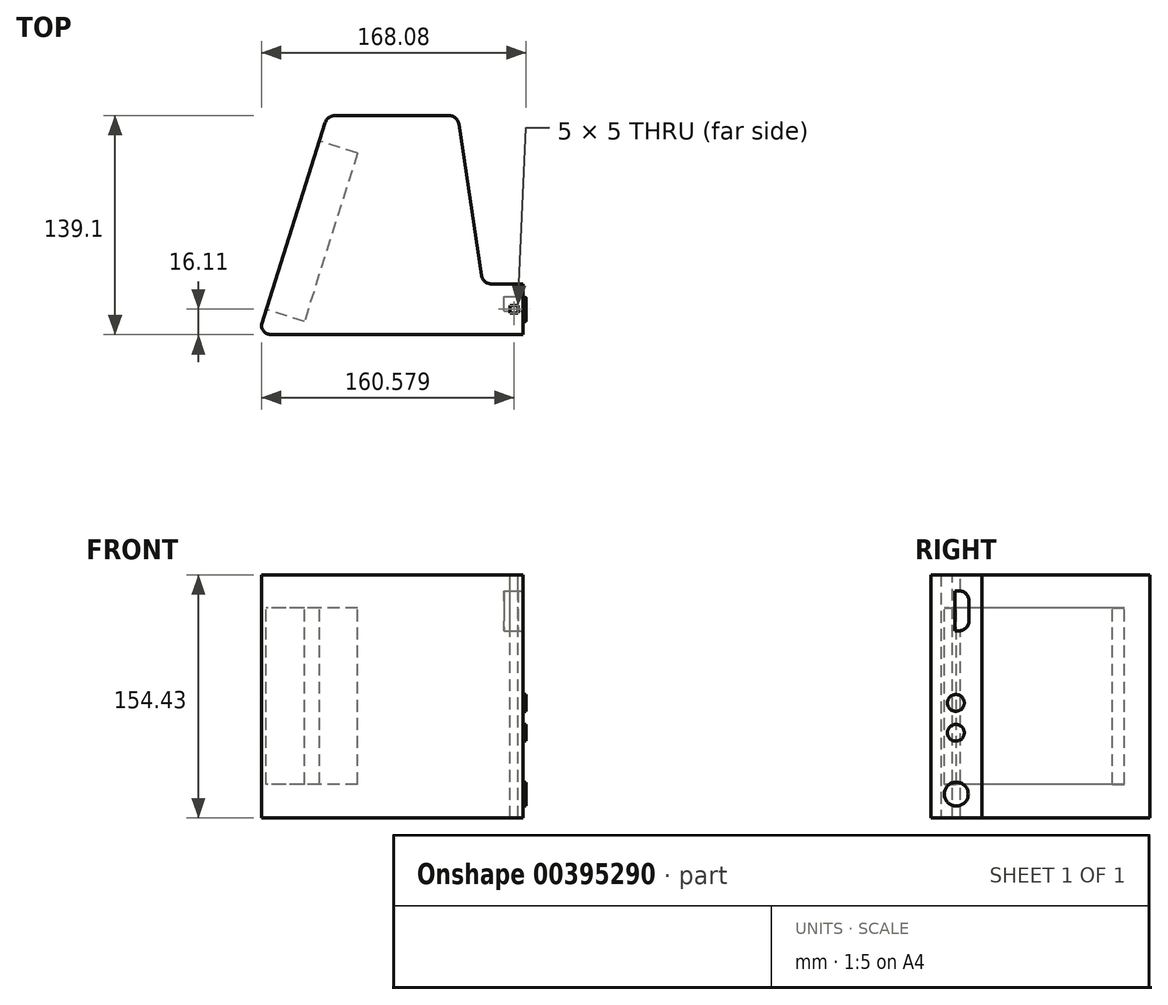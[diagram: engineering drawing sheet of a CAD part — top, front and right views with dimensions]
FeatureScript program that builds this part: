
annotation { "Feature Type Name" : "Feature", "Feature Type Description" : "" }
export const myFeature = defineFeature(function(context is Context, id is Id, definition is map)
    precondition{}
    {
        {
            var Q0;
            Q0=qCreatedBy(makeId("Top.planeOp"),FACE);
            var sketch = newSketch(context, id + "F0", { "sketchPlane" : qUnion([Q0])});
            skLineSegment(sketch, "E0", {"start": v(0, 0) * mm, "end": v(-134.26, 0) * mm});
            skLineSegment(sketch, "E1", {"start": v(5.47, 32.22) * mm, "end": v(22.47, 32.22) * mm});
            skLineSegment(sketch, "E2", {"start": v(0, 0) * mm, "end": v(22.47, 0) * mm});
            skPoint(sketch, "E3.visualSharp", {"position": v(-140.61, 0) * mm});
            skArc(sketch, "E3.filletArc", {"start": v(-140.61, 6.35) * mm, "mid": v(-138.75, 1.86) * mm, "end": v(-134.26, 0) * mm});
            skLineSegment(sketch, "E4", {"start": v(-140.61, 6.35) * mm, "end": v(-100.02, 134.66) * mm});
            skLineSegment(sketch, "E5", {"start": v(-93.96, 139.1) * mm, "end": v(-21.42, 139.1) * mm});
            skLineSegment(sketch, "E6", {"start": v(-15.14, 133.68) * mm, "end": v(-0.8, 37.63) * mm});
            skPoint(sketch, "E7.visualSharp", {"position": v(-98.61, 139.1) * mm});
            skArc(sketch, "E7.filletArc", {"start": v(-93.96, 139.1) * mm, "mid": v(-97.72, 137.87) * mm, "end": v(-100.02, 134.66) * mm});
            skPoint(sketch, "E8.visualSharp", {"position": v(-15.95, 139.1) * mm});
            skArc(sketch, "E8.filletArc", {"start": v(-15.14, 133.68) * mm, "mid": v(-17.27, 137.56) * mm, "end": v(-21.42, 139.1) * mm});
            skPoint(sketch, "E9.visualSharp", {"position": v(0, 32.22) * mm});
            skArc(sketch, "E9.filletArc", {"start": v(-0.8, 37.63) * mm, "mid": v(1.33, 33.76) * mm, "end": v(5.47, 32.22) * mm});
            skLineSegment(sketch, "E10.0", {"start": v(5.47, 25.87) * mm, "end": v(22.47, 25.87) * mm});
            skArc(sketch, "E10.1", {"start": v(-7.09, 36.7) * mm, "mid": v(-2.82, 28.95) * mm, "end": v(5.47, 25.87) * mm});
            skLineSegment(sketch, "E10.2", {"start": v(0, 6.35) * mm, "end": v(-128.75, 6.35) * mm});
            skLineSegment(sketch, "E10.3", {"start": v(-132.38, 11.3) * mm, "end": v(-94.8, 130.08) * mm});
            skLineSegment(sketch, "E10.4", {"start": v(-91.17, 132.75) * mm, "end": v(-24.7, 132.75) * mm});
            skLineSegment(sketch, "E10.5", {"start": v(-20.94, 129.5) * mm, "end": v(-7.09, 36.7) * mm});
            skLineSegment(sketch, "E11.0", {"start": v(0, 6.35) * mm, "end": v(22.47, 6.35) * mm});
            skLineSegment(sketch, "E12", {"start": v(22.47, 32.22) * mm, "end": v(22.47, 25.87) * mm});
            skLineSegment(sketch, "E13", {"start": v(22.47, 6.35) * mm, "end": v(22.47, 0) * mm});
            skArc(sketch, "E14.filletArc", {"start": v(-20.94, 129.5) * mm, "mid": v(-22.22, 131.82) * mm, "end": v(-24.7, 132.75) * mm});
            skArc(sketch, "E15.filletArc", {"start": v(-91.17, 132.75) * mm, "mid": v(-93.42, 132) * mm, "end": v(-94.8, 130.08) * mm});
            skPoint(sketch, "E16.visualSharp", {"position": v(-133.95, 6.35) * mm});
            skArc(sketch, "E16.filletArc", {"start": v(-132.38, 11.3) * mm, "mid": v(-131.83, 7.9) * mm, "end": v(-128.75, 6.35) * mm});
            skSolve(sketch);
        }
        {
            var Q0;
            Q0 = qSketchRegion(id + "F0", true);
            extrude(context, id + "F1", {"entities" : qUnion([Q0]), "depth" : 152.4 * mm});
        }
        {
            var Q0;
            Q0=makeQuery(id+"F1.opExtrude","CAP_FACE",FACE,{"disambiguationData":[OSD([sQuery(id+"F0.wireOp",EDGE,"E0"),sQuery(id+"F0.wireOp",EDGE,"E1"),sQuery(id+"F0.wireOp",EDGE,"E2"),sQuery(id+"F0.wireOp",EDGE,"E3.filletArc"),sQuery(id+"F0.wireOp",EDGE,"E4"),sQuery(id+"F0.wireOp",EDGE,"E5"),sQuery(id+"F0.wireOp",EDGE,"E6"),sQuery(id+"F0.wireOp",EDGE,"E7.filletArc"),sQuery(id+"F0.wireOp",EDGE,"E8.filletArc"),sQuery(id+"F0.wireOp",EDGE,"E9.filletArc"),sQuery(id+"F0.wireOp",EDGE,"E10.0"),sQuery(id+"F0.wireOp",EDGE,"E10.1"),sQuery(id+"F0.wireOp",EDGE,"E10.2"),sQuery(id+"F0.wireOp",EDGE,"E10.3"),sQuery(id+"F0.wireOp",EDGE,"E10.4"),sQuery(id+"F0.wireOp",EDGE,"E10.5"),sQuery(id+"F0.wireOp",EDGE,"E11.0"),sQuery(id+"F0.wireOp",EDGE,"E12"),sQuery(id+"F0.wireOp",EDGE,"E13"),sQuery(id+"F0.wireOp",EDGE,"E14.filletArc"),sQuery(id+"F0.wireOp",EDGE,"E15.filletArc"),sQuery(id+"F0.wireOp",EDGE,"E16.filletArc")])],"isStart":false});
            var sketch = newSketch(context, id + "F2", { "sketchPlane" : qUnion([Q0])});
            skLineSegment(sketch, "E17", {"start": v(0, 0) * mm, "end": v(-134.26, 0) * mm});
            skLineSegment(sketch, "E18", {"start": v(0, 0) * mm, "end": v(22.47, 0) * mm});
            skPoint(sketch, "E19.visualSharp", {"position": v(-140.61, 0) * mm});
            skArc(sketch, "E19.filletArc", {"start": v(-140.61, 6.35) * mm, "mid": v(-138.75, 1.86) * mm, "end": v(-134.26, 0) * mm});
            skLineSegment(sketch, "E20", {"start": v(-140.61, 6.35) * mm, "end": v(-100.02, 134.66) * mm});
            skLineSegment(sketch, "E21", {"start": v(-93.96, 139.1) * mm, "end": v(-21.42, 139.1) * mm});
            skLineSegment(sketch, "E22", {"start": v(-15.14, 133.68) * mm, "end": v(-0.8, 37.63) * mm});
            skPoint(sketch, "E23.visualSharp", {"position": v(-98.61, 139.1) * mm});
            skArc(sketch, "E23.filletArc", {"start": v(-93.96, 139.1) * mm, "mid": v(-97.72, 137.87) * mm, "end": v(-100.02, 134.66) * mm});
            skPoint(sketch, "E24.visualSharp", {"position": v(-15.95, 139.1) * mm});
            skArc(sketch, "E24.filletArc", {"start": v(-15.14, 133.68) * mm, "mid": v(-17.27, 137.56) * mm, "end": v(-21.42, 139.1) * mm});
            skPoint(sketch, "E25.visualSharp", {"position": v(-0.47, 35.35) * mm});
            skArc(sketch, "E25.filletArc", {"start": v(-0.8, 37.63) * mm, "mid": v(1.33, 33.76) * mm, "end": v(5.47, 32.22) * mm});
            skPoint(sketch, "E26.visualSharp", {"position": v(-133.95, 6.35) * mm});
            skLineSegment(sketch, "E27", {"start": v(5.47, 32.22) * mm, "end": v(22.47, 32.22) * mm});
            skLineSegment(sketch, "E28", {"start": v(22.47, 32.22) * mm, "end": v(22.47, 18.61) * mm});
            skLineSegment(sketch, "E29", {"start": v(22.47, 18.61) * mm, "end": v(17.47, 18.61) * mm});
            skLineSegment(sketch, "E30", {"start": v(17.47, 18.61) * mm, "end": v(17.47, 13.61) * mm});
            skLineSegment(sketch, "E31", {"start": v(17.47, 13.61) * mm, "end": v(22.47, 13.61) * mm});
            skLineSegment(sketch, "E32", {"start": v(22.47, 13.61) * mm, "end": v(22.47, 0) * mm});
            skSolve(sketch);
        }
        {
            var Q0;
            Q0 = qSketchRegion(id + "F2", true);
            extrude(context, id + "F3", {"entities" : qUnion([Q0]), "operationType" : NewBodyOperationType.ADD, "oppositeDirection" : true, "depth" : 154.43 * mm});
        }
        {
            var Q0;
            Q0=makeQuery(id+"F3.boolean.opBoolean","MERGE",FACE,{"derivedFrom":[makeQuery(id+"F1.opExtrude","SWEPT_FACE",FACE,{"disambiguationData":[OSD([sQuery(id+"F0.wireOp",EDGE,"E12")])]}),makeQuery(id+"F3.opExtrude","SWEPT_FACE",FACE,{"disambiguationData":[OSD([sQuery(id+"F2.wireOp",EDGE,"E28")])]})]});
            var sketch = newSketch(context, id + "F4", { "sketchPlane" : qUnion([Q0])});
            skPoint(sketch, "E33.firstSnap0", {"position": v(25.42, 152.4) * mm});
            skLineSegment(sketch, "E33.bottom", {"start": v(0, 152.4) * mm, "end": v(32.22, 152.4) * mm});
            skLineSegment(sketch, "E33.top", {"start": v(0, -2.03) * mm, "end": v(32.22, -2.03) * mm});
            skLineSegment(sketch, "E33.left", {"start": v(0, 152.4) * mm, "end": v(0, -2.03) * mm});
            skLineSegment(sketch, "E33.right", {"start": v(32.22, 152.4) * mm, "end": v(32.22, -2.03) * mm});
            skSolve(sketch);
        }
        {
            var Q0;
            Q0 = qSketchRegion(id + "F4", true);
            extrude(context, id + "F5", {"entities" : qUnion([Q0]), "operationType" : NewBodyOperationType.ADD, "depth" : 3 * mm});
        }
        {
            var Q0;
            Q0=makeQuery(id+"F5.opExtrude","CAP_FACE",FACE,{"disambiguationData":[OSD([sQuery(id+"F4.wireOp",EDGE,"E33.bottom"),sQuery(id+"F4.wireOp",EDGE,"E33.top"),sQuery(id+"F4.wireOp",EDGE,"E33.left"),sQuery(id+"F4.wireOp",EDGE,"E33.right")])],"isStart":false});
            var sketch = newSketch(context, id + "F6", { "sketchPlane" : qUnion([Q0])});
            skCircle(sketch, "E34", {"center": v(16.07, 13.06) * mm, "radius": 7.6 * mm});
            skCircle(sketch, "E35", {"center": v(15.81, 52.03) * mm, "radius": 5.33 * mm});
            skCircle(sketch, "E36", {"center": v(15.81, 70.99) * mm, "radius": 5.33 * mm});
            skSolve(sketch);
        }
        {
            var Q0;
            Q0 = qSketchRegion(id + "F6", true);
            extrude(context, id + "F7", {"entities" : qUnion([Q0]), "operationType" : NewBodyOperationType.ADD, "depth" : 2 * mm});
        }
        {
            var Q0;
            Q0=makeQuery(id+"F5.opExtrude","CAP_FACE",FACE,{"disambiguationData":[OSD([sQuery(id+"F4.wireOp",EDGE,"E33.bottom"),sQuery(id+"F4.wireOp",EDGE,"E33.top"),sQuery(id+"F4.wireOp",EDGE,"E33.left"),sQuery(id+"F4.wireOp",EDGE,"E33.right")])],"isStart":false});
            var sketch = newSketch(context, id + "F8", { "sketchPlane" : qUnion([Q0])});
            skLineSegment(sketch, "E37.bottom", {"start": v(15.12, 142.17) * mm, "end": v(17.77, 142.17) * mm});
            skLineSegment(sketch, "E37.top", {"start": v(15.12, 116.75) * mm, "end": v(17.77, 116.75) * mm});
            skLineSegment(sketch, "E37.left", {"start": v(15.12, 142.17) * mm, "end": v(15.12, 116.75) * mm});
            skLineSegment(sketch, "E37.right", {"start": v(24.12, 135.82) * mm, "end": v(24.12, 123.1) * mm});
            skPoint(sketch, "E38.visualSharp", {"position": v(24.12, 142.17) * mm});
            skArc(sketch, "E38.filletArc", {"start": v(24.12, 135.82) * mm, "mid": v(22.26, 140.31) * mm, "end": v(17.77, 142.17) * mm});
            skPoint(sketch, "E39.visualSharp", {"position": v(24.12, 116.75) * mm});
            skArc(sketch, "E39.filletArc", {"start": v(17.77, 116.75) * mm, "mid": v(22.26, 118.6) * mm, "end": v(24.12, 123.1) * mm});
            skSolve(sketch);
        }
        {
            var Q0;
            Q0 = qSketchRegion(id + "F8", true);
            extrude(context, id + "F9", {"entities" : qUnion([Q0]), "operationType" : NewBodyOperationType.REMOVE, "oppositeDirection" : true, "depth" : 12 * mm});
        }
        {
            var Q0;
            Q0=makeQuery(id+"F3.boolean.opBoolean","MERGE",FACE,{"derivedFrom":[makeQuery(id+"F1.opExtrude","SWEPT_FACE",FACE,{"disambiguationData":[OSD([sQuery(id+"F0.wireOp",EDGE,"E4")])]}),makeQuery(id+"F3.opExtrude","SWEPT_FACE",FACE,{"disambiguationData":[OSD([sQuery(id+"F2.wireOp",EDGE,"E20")])]})]});
            var sketch = newSketch(context, id + "F10", { "sketchPlane" : qUnion([Q0])});
            skLineSegment(sketch, "E40.bottom", {"start": v(-85.85, 19.37) * mm, "end": v(26.16, 19.37) * mm});
            skLineSegment(sketch, "E40.top", {"start": v(-85.85, 131.38) * mm, "end": v(26.16, 131.38) * mm});
            skLineSegment(sketch, "E40.left", {"start": v(-85.85, 19.37) * mm, "end": v(-85.85, 131.38) * mm});
            skLineSegment(sketch, "E40.right", {"start": v(26.16, 19.37) * mm, "end": v(26.16, 131.38) * mm});
            skSolve(sketch);
        }
        {
            var Q0;
            Q0=makeQuery(id+"F10.imprint","IMPRINT",FACE,{"disambiguationData":[TD([[makeQuery(id+"F10.imprint","IMPRINT",EDGE,{"derivedFrom":sQuery(id+"F10.wireOp",EDGE,"E40.bottom")}),1.0]])]});
            extrude(context, id + "F11", {"entities" : qUnion([Q0]), "operationType" : NewBodyOperationType.REMOVE, "oppositeDirection" : true, "depth" : 25.4 * mm});
        }
    });
